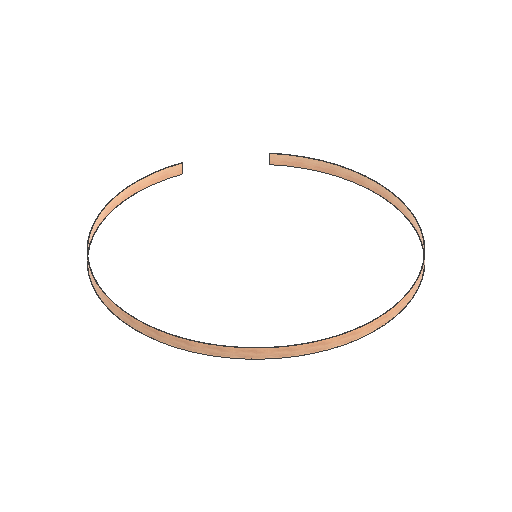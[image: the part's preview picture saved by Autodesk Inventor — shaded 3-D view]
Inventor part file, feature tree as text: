
AUTODESK INVENTOR PART (.ipt)
format: ipt  version: 2021 (Build 250183000, 183)  size: 115,200 bytes
history: native  units: mm
features: other x4, extrude x2, sketch x2, reference x2
ambient origin geometry x8: Origin, YZ Plane, XZ Plane, XY Plane, X Axis, Y Axis, Z Axis, Center Point
bodies: Solid1 (feature_tree)
feature tree (10):
  extrude  "Extrusion1"  Depth=2445.62mm
  extrude  "Extrusion2"  Depth=100.0mm TaperAngle=0.0deg
  sketch  "Sketch1"  dims[d0=2437.62mm d1=2445.62mm]
  sketch  "Sketch2"  dims[d2=100.0mm d3=0.0mm d4=100.0mm d5=0.0mm]
  reference  "Reference1"
  reference  "Reference2"
  other  "Full Scale Assembly.iam"
  other  "Disc C Assembly:1"
  other  "Platform C4:1"
  other  "Platform C1:1"
